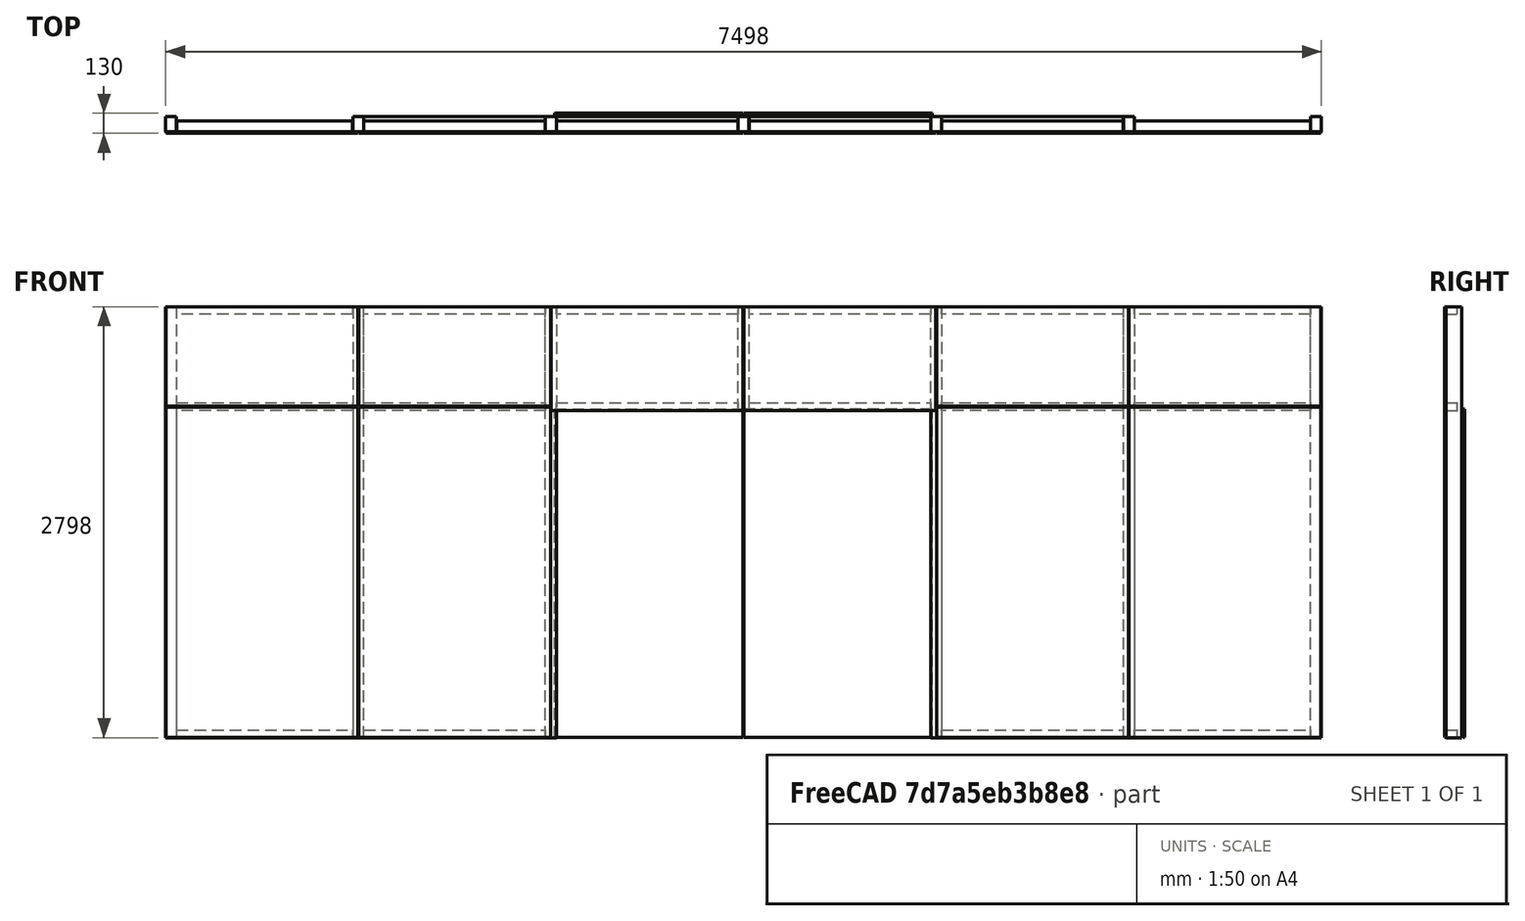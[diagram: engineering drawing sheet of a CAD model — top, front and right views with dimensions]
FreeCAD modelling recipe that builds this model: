
FCSTD DOCUMENT  (FreeCAD 0.16R6704 (Git))
Label: Glass skin 6 modules and sliding doors
License: CreativeCommons Attribution
LicenseURL: http://creativecommons.org/licenses/by/4.0/
objects: Sketcher::SketchObject×1, Part::FeaturePython×1
note: 2 computed .brp shape members not serialized (recipe doc carries the construction recipe); baked Part::Feature solids carry a one-line shape summary decoded from their .brp

FEATURE [Sketcher::SketchObject] Sketch206  label="Esboço pele de vidro 001"
  Placement = pos=(0,0,0) rot=(1,0,0;1.5708rad)
  sketch-geometry (176):
    g0: LineSegment StartX=0 StartY=0 StartZ=0 EndX=7500 EndY=0 EndZ=0
    g1: LineSegment StartX=7500 StartY=0 StartZ=0 EndX=7500 EndY=2800 EndZ=0
    g2: LineSegment StartX=7500 StartY=2800 StartZ=0 EndX=0 EndY=2800 EndZ=0
    g3: LineSegment StartX=0 StartY=2800 StartZ=0 EndX=0 EndY=0 EndZ=0
    g4: LineSegment StartX=1 StartY=2799 StartZ=0 EndX=71 EndY=2799 EndZ=0
    g5: LineSegment StartX=71 StartY=2799 StartZ=0 EndX=71 EndY=1 EndZ=0
    g6: LineSegment StartX=71 StartY=1 StartZ=0 EndX=1 EndY=1 EndZ=0
    g7: LineSegment StartX=1 StartY=1 StartZ=0 EndX=1 EndY=2799 EndZ=0
    g8: LineSegment StartX=1285 StartY=2799 StartZ=0 EndX=1215 EndY=2799 EndZ=0
    g9: LineSegment StartX=1215 StartY=2799 StartZ=0 EndX=1215 EndY=1 EndZ=0
    g10: LineSegment StartX=1215 StartY=1 StartZ=0 EndX=1285 EndY=1 EndZ=0
    g11: LineSegment StartX=1285 StartY=1 StartZ=0 EndX=1285 EndY=2799 EndZ=0
    g12: LineSegment StartX=72 StartY=2799 StartZ=0 EndX=1214 EndY=2799 EndZ=0
    g13: LineSegment StartX=1214 StartY=2799 StartZ=0 EndX=1214 EndY=2749 EndZ=0
    g14: LineSegment StartX=1214 StartY=2749 StartZ=0 EndX=72 EndY=2749 EndZ=0
    g15: LineSegment StartX=72 StartY=2749 StartZ=0 EndX=72 EndY=2799 EndZ=0
    g16: LineSegment StartX=72 StartY=2175 StartZ=0 EndX=1214 EndY=2175 EndZ=0
    g17: LineSegment StartX=1214 StartY=2175 StartZ=0 EndX=1214 EndY=2125 EndZ=0
    g18: LineSegment StartX=1214 StartY=2125 StartZ=0 EndX=72 EndY=2125 EndZ=0
    g19: LineSegment StartX=72 StartY=2125 StartZ=0 EndX=72 EndY=2175 EndZ=0
    g20: LineSegment StartX=72 StartY=51 StartZ=0 EndX=1214 EndY=51 EndZ=0
    g21: LineSegment StartX=1214 StartY=51 StartZ=0 EndX=1214 EndY=1 EndZ=0
    g22: LineSegment StartX=1214 StartY=1 StartZ=0 EndX=72 EndY=1 EndZ=0
    g23: LineSegment StartX=72 StartY=1 StartZ=0 EndX=72 EndY=51 EndZ=0
    g24: LineSegment [constr] StartX=0 StartY=4045.56 StartZ=0 EndX=0 EndY=0 EndZ=0
    g25: LineSegment [constr] StartX=1250 StartY=4032 StartZ=0 EndX=1250 EndY=-1064.23 EndZ=0
    g26: LineSegment [constr] StartX=2500 StartY=4059.26 StartZ=0 EndX=2500 EndY=-1119 EndZ=0
    g27: LineSegment [constr] StartX=3750 StartY=3908.57 StartZ=0 EndX=3750 EndY=-1023 EndZ=0
    g28: LineSegment [constr] StartX=5000 StartY=3990.77 StartZ=0 EndX=5000 EndY=-934.695 EndZ=0
    g29: LineSegment [constr] StartX=6250 StartY=4286.35 StartZ=0 EndX=6250 EndY=-1160 EndZ=0
    g30: LineSegment [constr] StartX=7500 StartY=4004.47 StartZ=0 EndX=7500 EndY=0 EndZ=0
    g31: LineSegment [constr] StartX=973.983 StartY=2150 StartZ=0 EndX=-10832.6 EndY=2150 EndZ=0
    g32: LineSegment [constr] StartX=0 StartY=3388 StartZ=0 EndX=1250 EndY=3388 EndZ=0
    g33: LineSegment [constr] StartX=1250 StartY=3579.79 StartZ=0 EndX=2500 EndY=3579.79 EndZ=0
    g34: LineSegment [constr] StartX=2500 StartY=3223.61 StartZ=0 EndX=3750 EndY=3223.61 EndZ=0
    g35: LineSegment [constr] StartX=3750 StartY=3538.69 StartZ=0 EndX=5000 EndY=3538.69 EndZ=0
    g36: LineSegment [constr] StartX=5000 StartY=3210 StartZ=0 EndX=6250 EndY=3210 EndZ=0
    g37: LineSegment [constr] StartX=6250 StartY=3579.79 StartZ=0 EndX=7500 EndY=3579.79 EndZ=0
    g38: LineSegment [constr] StartX=287.264 StartY=2799 StartZ=0 EndX=287.264 EndY=2749 EndZ=0
    g39: LineSegment [constr] StartX=559.643 StartY=2175 StartZ=0 EndX=559.643 EndY=2125 EndZ=0
    g40: LineSegment [constr] StartX=1 StartY=2367.03 StartZ=0 EndX=71 EndY=2367.03 EndZ=0
    g41: LineSegment [constr] StartX=1215 StartY=2396.22 StartZ=0 EndX=1285 EndY=2396.22 EndZ=0
    g42: LineSegment [constr] StartX=456.696 StartY=51 StartZ=0 EndX=456.696 EndY=1 EndZ=0
    g43: LineSegment StartX=2.5 StartY=2797.5 StartZ=0 EndX=1247.5 EndY=2797.5 EndZ=0
    g44: LineSegment StartX=1247.5 StartY=2797.5 StartZ=0 EndX=1247.5 EndY=2152.5 EndZ=0
    g45: LineSegment StartX=1247.5 StartY=2152.5 StartZ=0 EndX=2.5 EndY=2152.5 EndZ=0
    g46: LineSegment StartX=2.5 StartY=2152.5 StartZ=0 EndX=2.5 EndY=2797.5 EndZ=0
    g47: LineSegment StartX=2465 StartY=2799 StartZ=0 EndX=2535 EndY=2799 EndZ=0
    g48: LineSegment StartX=2535 StartY=2799 StartZ=0 EndX=2535 EndY=1 EndZ=0
    g49: LineSegment StartX=2535 StartY=1 StartZ=0 EndX=2465 EndY=1 EndZ=0
    g50: LineSegment StartX=2465 StartY=1 StartZ=0 EndX=2465 EndY=2799 EndZ=0
    g51: LineSegment StartX=3715 StartY=2799 StartZ=0 EndX=3785 EndY=2799 EndZ=0
    g52: LineSegment StartX=3785 StartY=2799 StartZ=0 EndX=3785 EndY=2125 EndZ=0
    g53: LineSegment StartX=3785 StartY=2125 StartZ=0 EndX=3715 EndY=2125 EndZ=0
    g54: LineSegment StartX=3715 StartY=2125 StartZ=0 EndX=3715 EndY=2799 EndZ=0
    g55: LineSegment StartX=4965 StartY=2799 StartZ=0 EndX=5035 EndY=2799 EndZ=0
    g56: LineSegment StartX=5035 StartY=2799 StartZ=0 EndX=5035 EndY=1 EndZ=0
    g57: LineSegment StartX=5035 StartY=1 StartZ=0 EndX=4965 EndY=1 EndZ=0
    g58: LineSegment StartX=4965 StartY=1 StartZ=0 EndX=4965 EndY=2799 EndZ=0
    g59: LineSegment StartX=6215 StartY=2799 StartZ=0 EndX=6285 EndY=2799 EndZ=0
    g60: LineSegment StartX=6285 StartY=2799 StartZ=0 EndX=6285 EndY=1 EndZ=0
    g61: LineSegment StartX=6285 StartY=1 StartZ=0 EndX=6215 EndY=1 EndZ=0
    g62: LineSegment StartX=6215 StartY=1 StartZ=0 EndX=6215 EndY=2799 EndZ=0
    g63: LineSegment StartX=7429 StartY=2799 StartZ=0 EndX=7499 EndY=2799 EndZ=0
    g64: LineSegment StartX=7499 StartY=2799 StartZ=0 EndX=7499 EndY=1 EndZ=0
    g65: LineSegment StartX=7499 StartY=1 StartZ=0 EndX=7429 EndY=1 EndZ=0
    g66: LineSegment StartX=7429 StartY=1 StartZ=0 EndX=7429 EndY=2799 EndZ=0
    g67: LineSegment [constr] StartX=2465 StartY=1674.46 StartZ=0 EndX=2535 EndY=1674.46 EndZ=0
    g68: LineSegment [constr] StartX=3715 StartY=1674.45 StartZ=0 EndX=3785 EndY=1674.45 EndZ=0
    g69: LineSegment [constr] StartX=4965 StartY=1669.74 StartZ=0 EndX=5035 EndY=1669.74 EndZ=0
    g70: LineSegment [constr] StartX=6215 StartY=1602 StartZ=0 EndX=6285 EndY=1602 EndZ=0
    g71: LineSegment [constr] StartX=7429 StartY=1550.78 StartZ=0 EndX=7499 EndY=1550.78 EndZ=0
    g72: LineSegment StartX=1286 StartY=2799 StartZ=0 EndX=2464 EndY=2799 EndZ=0
    g73: LineSegment StartX=2464 StartY=2799 StartZ=0 EndX=2464 EndY=2749 EndZ=0
    g74: LineSegment StartX=2464 StartY=2749 StartZ=0 EndX=1286 EndY=2749 EndZ=0
    g75: LineSegment StartX=1286 StartY=2749 StartZ=0 EndX=1286 EndY=2799 EndZ=0
    g76: LineSegment StartX=1286 StartY=2175 StartZ=0 EndX=2464 EndY=2175 EndZ=0
    g77: LineSegment StartX=2464 StartY=2175 StartZ=0 EndX=2464 EndY=2125 EndZ=0
    g78: LineSegment StartX=2464 StartY=2125 StartZ=0 EndX=1286 EndY=2125 EndZ=0
    g79: LineSegment StartX=1286 StartY=2125 StartZ=0 EndX=1286 EndY=2175 EndZ=0
    g80: LineSegment StartX=1286 StartY=51 StartZ=0 EndX=2464 EndY=51 EndZ=0
    g81: LineSegment StartX=2464 StartY=51 StartZ=0 EndX=2464 EndY=1 EndZ=0
    g82: LineSegment StartX=2464 StartY=1 StartZ=0 EndX=1286 EndY=1 EndZ=0
    g83: LineSegment StartX=1286 StartY=1 StartZ=0 EndX=1286 EndY=51 EndZ=0
    g84: LineSegment StartX=1252.5 StartY=2797.5 StartZ=0 EndX=2497.5 EndY=2797.5 EndZ=0
    g85: LineSegment StartX=2497.5 StartY=2797.5 StartZ=0 EndX=2497.5 EndY=2152.5 EndZ=0
    g86: LineSegment StartX=2497.5 StartY=2152.5 StartZ=0 EndX=1252.5 EndY=2152.5 EndZ=0
    g87: LineSegment StartX=1252.5 StartY=2152.5 StartZ=0 EndX=1252.5 EndY=2797.5 EndZ=0
    g88: LineSegment StartX=2536 StartY=2799 StartZ=0 EndX=3714 EndY=2799 EndZ=0
    g89: LineSegment StartX=3714 StartY=2799 StartZ=0 EndX=3714 EndY=2749 EndZ=0
    g90: LineSegment StartX=3714 StartY=2749 StartZ=0 EndX=2536 EndY=2749 EndZ=0
    g91: LineSegment StartX=2536 StartY=2749 StartZ=0 EndX=2536 EndY=2799 EndZ=0
    g92: LineSegment StartX=2536 StartY=2175 StartZ=0 EndX=3714 EndY=2175 EndZ=0
    g93: LineSegment StartX=3714 StartY=2175 StartZ=0 EndX=3714 EndY=2125 EndZ=0
    g94: LineSegment StartX=3714 StartY=2125 StartZ=0 EndX=2536 EndY=2125 EndZ=0
    g95: LineSegment StartX=2536 StartY=2125 StartZ=0 EndX=2536 EndY=2175 EndZ=0
    g96: LineSegment StartX=2536 StartY=51 StartZ=0 EndX=3714 EndY=51 EndZ=0
    g97: LineSegment StartX=3714 StartY=51 StartZ=0 EndX=3714 EndY=1 EndZ=0
    g98: LineSegment StartX=3714 StartY=1 StartZ=0 EndX=2536 EndY=1 EndZ=0
    g99: LineSegment StartX=2536 StartY=1 StartZ=0 EndX=2536 EndY=51 EndZ=0
    g100: LineSegment StartX=3786 StartY=2799 StartZ=0 EndX=4964 EndY=2799 EndZ=0
    g101: LineSegment StartX=4964 StartY=2799 StartZ=0 EndX=4964 EndY=2749 EndZ=0
    g102: LineSegment StartX=4964 StartY=2749 StartZ=0 EndX=3786 EndY=2749 EndZ=0
    g103: LineSegment StartX=3786 StartY=2749 StartZ=0 EndX=3786 EndY=2799 EndZ=0
    g104: LineSegment StartX=3786 StartY=2175 StartZ=0 EndX=4964 EndY=2175 EndZ=0
    g105: LineSegment StartX=4964 StartY=2175 StartZ=0 EndX=4964 EndY=2125 EndZ=0
    g106: LineSegment StartX=4964 StartY=2125 StartZ=0 EndX=3786 EndY=2125 EndZ=0
    g107: LineSegment StartX=3786 StartY=2125 StartZ=0 EndX=3786 EndY=2175 EndZ=0
    g108: LineSegment StartX=3786 StartY=51 StartZ=0 EndX=4964 EndY=51 EndZ=0
    g109: LineSegment StartX=4964 StartY=51 StartZ=0 EndX=4964 EndY=1 EndZ=0
    g110: LineSegment StartX=4964 StartY=1 StartZ=0 EndX=3786 EndY=1 EndZ=0
    g111: LineSegment StartX=3786 StartY=1 StartZ=0 EndX=3786 EndY=51 EndZ=0
    g112: LineSegment StartX=5036 StartY=2799 StartZ=0 EndX=6214 EndY=2799 EndZ=0
    g113: LineSegment StartX=6214 StartY=2799 StartZ=0 EndX=6214 EndY=2749 EndZ=0
    g114: LineSegment StartX=6214 StartY=2749 StartZ=0 EndX=5036 EndY=2749 EndZ=0
    g115: LineSegment StartX=5036 StartY=2749 StartZ=0 EndX=5036 EndY=2799 EndZ=0
    g116: LineSegment StartX=5036 StartY=2175 StartZ=0 EndX=6214 EndY=2175 EndZ=0
    g117: LineSegment StartX=6214 StartY=2175 StartZ=0 EndX=6214 EndY=2125 EndZ=0
    g118: LineSegment StartX=6214 StartY=2125 StartZ=0 EndX=5036 EndY=2125 EndZ=0
    g119: LineSegment StartX=5036 StartY=2125 StartZ=0 EndX=5036 EndY=2175 EndZ=0
    g120: LineSegment StartX=5036 StartY=51 StartZ=0 EndX=6214 EndY=51 EndZ=0
    g121: LineSegment StartX=6214 StartY=51 StartZ=0 EndX=6214 EndY=1 EndZ=0
    g122: LineSegment StartX=6214 StartY=1 StartZ=0 EndX=5036 EndY=1 EndZ=0
    g123: LineSegment StartX=5036 StartY=1 StartZ=0 EndX=5036 EndY=51 EndZ=0
    g124: LineSegment StartX=6286 StartY=2799 StartZ=0 EndX=7428 EndY=2799 EndZ=0
    g125: LineSegment StartX=7428 StartY=2799 StartZ=0 EndX=7428 EndY=2749 EndZ=0
    g126: LineSegment StartX=7428 StartY=2749 StartZ=0 EndX=6286 EndY=2749 EndZ=0
    g127: LineSegment StartX=6286 StartY=2749 StartZ=0 EndX=6286 EndY=2799 EndZ=0
    g128: LineSegment StartX=6286 StartY=2175 StartZ=0 EndX=7428 EndY=2175 EndZ=0
    g129: LineSegment StartX=7428 StartY=2175 StartZ=0 EndX=7428 EndY=2125 EndZ=0
    g130: LineSegment StartX=7428 StartY=2125 StartZ=0 EndX=6286 EndY=2125 EndZ=0
    g131: LineSegment StartX=6286 StartY=2125 StartZ=0 EndX=6286 EndY=2175 EndZ=0
    g132: LineSegment StartX=6286 StartY=51 StartZ=0 EndX=7428 EndY=51 EndZ=0
    g133: LineSegment StartX=7428 StartY=51 StartZ=0 EndX=7428 EndY=1 EndZ=0
    g134: LineSegment StartX=7428 StartY=1 StartZ=0 EndX=6286 EndY=1 EndZ=0
    g135: LineSegment StartX=6286 StartY=1 StartZ=0 EndX=6286 EndY=51 EndZ=0
    g136: LineSegment StartX=2502.5 StartY=2797.5 StartZ=0 EndX=3747.5 EndY=2797.5 EndZ=0
    g137: LineSegment StartX=3747.5 StartY=2797.5 StartZ=0 EndX=3747.5 EndY=2125 EndZ=0
    g138: LineSegment StartX=3747.5 StartY=2125 StartZ=0 EndX=2502.5 EndY=2125 EndZ=0
    g139: LineSegment StartX=2502.5 StartY=2125 StartZ=0 EndX=2502.5 EndY=2797.5 EndZ=0
    g140: LineSegment StartX=3752.5 StartY=2125 StartZ=0 EndX=4997.5 EndY=2125 EndZ=0
    g141: LineSegment StartX=4997.5 StartY=2125 StartZ=0 EndX=4997.5 EndY=2797.5 EndZ=0
    g142: LineSegment StartX=4997.5 StartY=2797.5 StartZ=0 EndX=3752.5 EndY=2797.5 EndZ=0
    g143: LineSegment StartX=3752.5 StartY=2797.5 StartZ=0 EndX=3752.5 EndY=2125 EndZ=0
    g144: LineSegment StartX=5002.5 StartY=2797.5 StartZ=0 EndX=6247.5 EndY=2797.5 EndZ=0
    g145: LineSegment StartX=6247.5 StartY=2797.5 StartZ=0 EndX=6247.5 EndY=2152.5 EndZ=0
    g146: LineSegment StartX=6247.5 StartY=2152.5 StartZ=0 EndX=5002.5 EndY=2152.5 EndZ=0
    g147: LineSegment StartX=5002.5 StartY=2152.5 StartZ=0 EndX=5002.5 EndY=2797.5 EndZ=0
    g148: LineSegment StartX=6252.5 StartY=2152.5 StartZ=0 EndX=7497.5 EndY=2152.5 EndZ=0
    g149: LineSegment StartX=7497.5 StartY=2152.5 StartZ=0 EndX=7497.5 EndY=2797.5 EndZ=0
    g150: LineSegment StartX=7497.5 StartY=2797.5 StartZ=0 EndX=6252.5 EndY=2797.5 EndZ=0
    g151: LineSegment StartX=6252.5 StartY=2797.5 StartZ=0 EndX=6252.5 EndY=2152.5 EndZ=0
    g152: LineSegment StartX=2525 StartY=2135 StartZ=0 EndX=3747.5 EndY=2135 EndZ=0
    g153: LineSegment StartX=3747.5 StartY=2135 StartZ=0 EndX=3747.5 EndY=2.5 EndZ=0
    g154: LineSegment StartX=3747.5 StartY=2.5 StartZ=0 EndX=2525 EndY=2.5 EndZ=0
    g155: LineSegment StartX=2525 StartY=2.5 StartZ=0 EndX=2525 EndY=2135 EndZ=0
    g156: LineSegment StartX=3752.5 StartY=2.5 StartZ=0 EndX=4975 EndY=2.5 EndZ=0
    g157: LineSegment StartX=4975 StartY=2.5 StartZ=0 EndX=4975 EndY=2135 EndZ=0
    g158: LineSegment StartX=4975 StartY=2135 StartZ=0 EndX=3752.5 EndY=2135 EndZ=0
    g159: LineSegment StartX=3752.5 StartY=2135 StartZ=0 EndX=3752.5 EndY=2.5 EndZ=0
    g160: LineSegment StartX=2.5 StartY=2147.5 StartZ=0 EndX=1247.5 EndY=2147.5 EndZ=0
    g161: LineSegment StartX=1247.5 StartY=2147.5 StartZ=0 EndX=1247.5 EndY=2.5 EndZ=0
    g162: LineSegment StartX=1247.5 StartY=2.5 StartZ=0 EndX=2.5 EndY=2.5 EndZ=0
    g163: LineSegment StartX=2.5 StartY=2.5 StartZ=0 EndX=2.5 EndY=2147.5 EndZ=0
    g164: LineSegment StartX=1252.5 StartY=2147.5 StartZ=0 EndX=2497.5 EndY=2147.5 EndZ=0
    g165: LineSegment StartX=2497.5 StartY=2147.5 StartZ=0 EndX=2497.5 EndY=2.5 EndZ=0
    g166: LineSegment StartX=2497.5 StartY=2.5 StartZ=0 EndX=1252.5 EndY=2.5 EndZ=0
    g167: LineSegment StartX=1252.5 StartY=2.5 StartZ=0 EndX=1252.5 EndY=2147.5 EndZ=0
    g168: LineSegment StartX=5002.5 StartY=2147.5 StartZ=0 EndX=6247.5 EndY=2147.5 EndZ=0
    g169: LineSegment StartX=6247.5 StartY=2147.5 StartZ=0 EndX=6247.5 EndY=2.5 EndZ=0
    g170: LineSegment StartX=6247.5 StartY=2.5 StartZ=0 EndX=5002.5 EndY=2.5 EndZ=0
    g171: LineSegment StartX=5002.5 StartY=2.5 StartZ=0 EndX=5002.5 EndY=2147.5 EndZ=0
    g172: LineSegment StartX=6252.5 StartY=2147.5 StartZ=0 EndX=7497.5 EndY=2147.5 EndZ=0
    g173: LineSegment StartX=7497.5 StartY=2147.5 StartZ=0 EndX=7497.5 EndY=2.5 EndZ=0
    g174: LineSegment StartX=7497.5 StartY=2.5 StartZ=0 EndX=6252.5 EndY=2.5 EndZ=0
    g175: LineSegment StartX=6252.5 StartY=2.5 StartZ=0 EndX=6252.5 EndY=2147.5 EndZ=0
  constraints (510):
    c: Coincident(g0,g1)
    c: Coincident(g1,g2)
    c: Coincident(g2,g3)
    c: Coincident(g3,g0)
    c: Horizontal(g0)
    c: Horizontal(g2)
    c: Vertical(g1)
    c: Vertical(g3)
    c: Coincident(g0,g-1)
    c: DistanceX(g2,g1) = 7500  'Largura do vão'
    c: DistanceY(g-1,g2) = 2800  'Altura do vão'
    c: Coincident(g4,g5)
    c: Coincident(g5,g6)
    c: Coincident(g6,g7)
    c: Coincident(g7,g4)
    c: Horizontal(g4)
    c: Horizontal(g6)
    c: Vertical(g5)
    c: Vertical(g7)
    c: Coincident(g8,g9)
    c: Coincident(g9,g10)
    c: Coincident(g10,g11)
    c: Coincident(g11,g8)
    c: Horizontal(g8)
    c: Horizontal(g10)
    c: Vertical(g9)
    c: Vertical(g11)
    c: Coincident(g12,g13)
    c: Coincident(g13,g14)
    c: Coincident(g14,g15)
    c: Coincident(g15,g12)
    c: Horizontal(g12)
    c: Horizontal(g14)
    c: Vertical(g13)
    c: Vertical(g15)
    c: Coincident(g16,g17)
    c: Coincident(g17,g18)
    c: Coincident(g18,g19)
    c: Coincident(g19,g16)
    c: Horizontal(g16)
    c: Horizontal(g18)
    c: Vertical(g17)
    c: Vertical(g19)
    c: Coincident(g20,g21)
    c: Coincident(g21,g22)
    c: Coincident(g22,g23)
    c: Coincident(g23,g20)
    c: Horizontal(g20)
    c: Horizontal(g22)
    c: Vertical(g21)
    c: Vertical(g23)
    c: Vertical(g24)
    c: Vertical(g30)
    c: PointOnObject(g32,g24)
    c: PointOnObject(g32,g25)
    c: PointOnObject(g33,g25)
    c: PointOnObject(g33,g26)
    c: PointOnObject(g34,g26)
    c: PointOnObject(g34,g27)
    c: PointOnObject(g35,g27)
    c: PointOnObject(g35,g28)
    c: PointOnObject(g36,g28)
    c: PointOnObject(g36,g29)
    c: PointOnObject(g37,g29)
    c: PointOnObject(g37,g30)
    c: Equal(g32,g33)
    c: Equal(g33,g34)
    c: Equal(g34,g35)
    c: Equal(g35,g36)
    c: Equal(g36,g37)
    c: Angle(g32) = 0
    c: Angle(g33) = 0
    c: Angle(g34) = 0
    c: Angle(g35) = 0
    c: Angle(g36) = 0
    c: Angle(g37) = 0
    c: Coincident(g24,g-1)
    c: Coincident(g30,g0)
    c: DistanceY(g-1,g31) = 2150  'Altura da divisão horizontal (eixo)'
    c: Symmetric(g16,g18,g31)  'Constraint85'
    c: Symmetric(g8,g8,g25)  'Constraint84'
    c: DistanceY(g12,g2) = 1  'Constraint83'
    c: DistanceY(g14,g12) = 50  'Altura dos perfis horizontais'
    c: DistanceX(g16,g14) = 0  'Constraint88'
    c: PointOnObject(g38,g12)  'Constraint87'
    c: PointOnObject(g38,g14)  'Constraint86'
    c: PointOnObject(g39,g16)
    c: PointOnObject(g39,g18)
    c: Angle(g38) = -1.5708
    c: Angle(g39) = -1.5708
    c: DistanceX(g2,g4) = 1
    c: DistanceY(g4,g2) = 1
    c: DistanceY(g-1,g6) = 1
    c: DistanceX(g4,g4) = 70  'Largura perfis verticais'
    c: PointOnObject(g40,g7)  'Constraint101'
    c: PointOnObject(g40,g5)
    c: Angle(g40) = 0
    c: DistanceX(g4,g12) = 1
    c: PointOnObject(g41,g9)
    c: PointOnObject(g41,g11)
    c: Angle(g41) = 0
    c: DistanceY(g8,g4) = 0
    c: DistanceY(g5,g9) = 0
    c: PointOnObject(g42,g20)
    c: PointOnObject(g42,g22)
    c: Angle(g42) = -1.5708
    c: DistanceX(g20,g18) = 0
    c: DistanceY(g5,g22) = 0
    c: Equal(g38,g39)
    c: Equal(g39,g42)
    c: DistanceX(g12,g8) = 1
    c: DistanceX(g13,g16) = 0
    c: DistanceX(g17,g20) = 0
    c: Coincident(g43,g44)
    c: Coincident(g44,g45)
    c: Coincident(g45,g46)
    c: Coincident(g46,g43)
    c: Horizontal(g43)
    c: Horizontal(g45)
    c: Vertical(g44)
    c: Vertical(g46)
    c: DistanceY(g43,g4) = 1.5
    c: DistanceX(g4,g43) = 1.5
    c: Coincident(g47,g48)
    c: Coincident(g48,g49)
    c: Coincident(g49,g50)
    c: Coincident(g50,g47)
    c: Horizontal(g47)
    c: Horizontal(g49)
    c: Vertical(g48)
    c: Vertical(g50)
    c: Coincident(g51,g52)
    c: Coincident(g52,g53)
    c: Coincident(g53,g54)
    c: Coincident(g54,g51)
    c: Horizontal(g51)
    c: Horizontal(g53)
    c: Vertical(g52)
    c: Vertical(g54)
    c: Coincident(g55,g56)
    c: Coincident(g56,g57)
    c: Coincident(g57,g58)
    c: Coincident(g58,g55)
    c: Horizontal(g55)
    c: Horizontal(g57)
    c: Vertical(g56)
    c: Vertical(g58)
    c: Coincident(g59,g60)
    c: Coincident(g60,g61)
    c: Coincident(g61,g62)
    c: Coincident(g62,g59)
    c: Horizontal(g59)
    c: Horizontal(g61)
    c: Vertical(g60)
    c: Vertical(g62)
    c: Coincident(g63,g64)
    c: Coincident(g64,g65)
    c: Coincident(g65,g66)
    c: Coincident(g66,g63)
    c: Horizontal(g63)
    c: Horizontal(g65)
    c: Vertical(g64)
    c: Vertical(g66)
    c: DistanceY(g47,g8) = 0
    c: Symmetric(g47,g47,g26)
    c: DistanceY(g51,g47) = 0
    c: Symmetric(g51,g51,g27)
    c: DistanceY(g55,g51) = 0
    c: Symmetric(g55,g55,g28)
    c: DistanceY(g55,g59) = 0
    c: Symmetric(g59,g59,g29)
    c: DistanceY(g63,g59) = 0
    c: DistanceX(g63,g1) = 1
    c: DistanceY(g10,g49) = 0
    c: DistanceY(g56,g61) = 0
    c: DistanceY(g60,g65) = 0
    c: PointOnObject(g67,g50)
    c: PointOnObject(g67,g48)
    c: PointOnObject(g68,g54)
    c: PointOnObject(g68,g52)
    c: PointOnObject(g69,g58)
    c: PointOnObject(g69,g56)
    c: PointOnObject(g70,g62)
    c: PointOnObject(g70,g60)
    c: PointOnObject(g71,g66)
    c: PointOnObject(g71,g64)
    c: Angle(g71) = 0
    c: Angle(g70) = 0
    c: Angle(g69) = 0
    c: Angle(g68) = 0
    c: Angle(g67) = 0
    c: Equal(g40,g41)
    c: Equal(g41,g67)
    c: Equal(g67,g68)
    c: Equal(g68,g69)
    c: Equal(g69,g70)
    c: Equal(g70,g71)
    c: Coincident(g72,g73)
    c: Coincident(g73,g74)
    c: Coincident(g74,g75)
    c: Coincident(g75,g72)
    c: Horizontal(g72)
    c: Horizontal(g74)
    c: Vertical(g73)
    c: Vertical(g75)
    c: Coincident(g76,g77)
    c: Coincident(g77,g78)
    c: Coincident(g78,g79)
    c: Coincident(g79,g76)
    c: Horizontal(g76)
    c: Horizontal(g78)
    c: Vertical(g77)
    c: Vertical(g79)
    c: Coincident(g80,g81)
    c: Coincident(g81,g82)
    c: Coincident(g82,g83)
    c: Coincident(g83,g80)
    c: Horizontal(g80)
    c: Horizontal(g82)
    c: Vertical(g81)
    c: Vertical(g83)
    c: DistanceX(g8,g72) = 1
    c: DistanceY(g72,g12) = 0
    c: DistanceY(g74,g13) = 0
    c: DistanceX(g74,g76) = 0
    c: DistanceY(g16,g76) = 0
    c: DistanceY(g78,g17) = 0
    c: DistanceX(g78,g80) = 0
    c: DistanceY(g21,g82) = 0
    c: DistanceY(g20,g80) = 0
    c: DistanceX(g72,g47) = 1
    c: DistanceX(g76,g73) = 0
    c: DistanceX(g80,g77) = 0
    c: Coincident(g84,g85)
    c: Coincident(g85,g86)
    c: Coincident(g86,g87)
    c: Coincident(g87,g84)
    c: Horizontal(g84)
    c: Horizontal(g86)
    c: Vertical(g85)
    c: Vertical(g87)
    c: DistanceY(g84,g43) = 0
    c: DistanceY(g44,g86) = 0
    c: Symmetric(g44,g86,g25)
    c: DistanceX(g44,g86) = 5
    c: Coincident(g88,g89)
    c: Coincident(g89,g90)
    c: Coincident(g90,g91)
    c: Coincident(g91,g88)
    c: Horizontal(g88)
    c: Horizontal(g90)
    c: Vertical(g89)
    c: Vertical(g91)
    c: Coincident(g92,g93)
    c: Coincident(g93,g94)
    c: Coincident(g94,g95)
    c: Coincident(g95,g92)
    c: Horizontal(g92)
    c: Horizontal(g94)
    c: Vertical(g93)
    c: Vertical(g95)
    c: Coincident(g96,g97)
    c: Coincident(g97,g98)
    c: Coincident(g98,g99)
    c: Coincident(g99,g96)
    c: Horizontal(g96)
    c: Horizontal(g98)
    c: Vertical(g97)
    c: Vertical(g99)
    c: Coincident(g100,g101)
    c: Coincident(g101,g102)
    c: Coincident(g102,g103)
    c: Coincident(g103,g100)
    c: Horizontal(g100)
    c: Horizontal(g102)
    c: Vertical(g101)
    c: Vertical(g103)
    c: Coincident(g104,g105)
    c: Coincident(g105,g106)
    c: Coincident(g106,g107)
    c: Coincident(g107,g104)
    c: Horizontal(g104)
    c: Horizontal(g106)
    c: Vertical(g105)
    c: Vertical(g107)
    c: Coincident(g108,g109)
    c: Coincident(g109,g110)
    c: Coincident(g110,g111)
    c: Coincident(g111,g108)
    c: Horizontal(g108)
    c: Horizontal(g110)
    c: Vertical(g109)
    c: Vertical(g111)
    c: Coincident(g112,g113)
    c: Coincident(g113,g114)
    c: Coincident(g114,g115)
    c: Coincident(g115,g112)
    c: Horizontal(g112)
    c: Horizontal(g114)
    c: Vertical(g113)
    c: Vertical(g115)
    c: Coincident(g116,g117)
    c: Coincident(g117,g118)
    c: Coincident(g118,g119)
    c: Coincident(g119,g116)
    c: Horizontal(g116)
    c: Horizontal(g118)
    c: Vertical(g117)
    c: Vertical(g119)
    c: Coincident(g120,g121)
    c: Coincident(g121,g122)
    c: Coincident(g122,g123)
    c: Coincident(g123,g120)
    c: Horizontal(g120)
    c: Horizontal(g122)
    c: Vertical(g121)
    c: Vertical(g123)
    c: Coincident(g124,g125)
    c: Coincident(g125,g126)
    c: Coincident(g126,g127)
    c: Coincident(g127,g124)
    c: Horizontal(g124)
    c: Horizontal(g126)
    c: Vertical(g125)
    c: Vertical(g127)
    c: Coincident(g128,g129)
    c: Coincident(g129,g130)
    c: Coincident(g130,g131)
    c: Coincident(g131,g128)
    c: Horizontal(g128)
    c: Horizontal(g130)
    c: Vertical(g129)
    c: Vertical(g131)
    c: Coincident(g132,g133)
    c: Coincident(g133,g134)
    c: Coincident(g134,g135)
    c: Coincident(g135,g132)
    c: Horizontal(g132)
    c: Horizontal(g134)
    c: Vertical(g133)
    c: Vertical(g135)
    c: DistanceX(g47,g88) = 1
    c: DistanceY(g88,g72) = 0
    c: DistanceY(g90,g73) = 0
    c: DistanceX(g90,g92) = 0
    c: DistanceY(g76,g92) = 0
    c: DistanceY(g94,g77) = 0
    c: DistanceX(g94,g96) = 0
    c: DistanceY(g80,g96) = 0
    c: DistanceY(g81,g98) = 0
    c: DistanceX(g88,g51) = 1
    c: DistanceX(g92,g89) = 0
    c: DistanceX(g96,g93) = 0
    c: DistanceX(g51,g100) = 1
    c: DistanceY(g100,g88) = 0
    c: DistanceY(g102,g89) = 0
    c: DistanceX(g102,g104) = 0
    c: DistanceY(g92,g104) = 0
    c: DistanceY(g106,g93) = 0
    c: DistanceX(g106,g108) = 0
    c: DistanceY(g96,g108) = 0
    c: DistanceX(g100,g55) = 1
    c: DistanceX(g104,g101) = 0
    c: DistanceX(g108,g105) = 0
    c: DistanceX(g55,g112) = 1
    c: DistanceY(g112,g100) = 0
    c: DistanceY(g114,g101) = 0
    c: DistanceX(g114,g116) = 0
    c: DistanceY(g104,g116) = 0
    c: DistanceY(g118,g105) = 0
    c: DistanceX(g118,g120) = 0
    c: DistanceY(g108,g120) = 0
    c: DistanceX(g112,g59) = 1
    c: DistanceX(g116,g113) = 0
    c: DistanceX(g120,g117) = 0
    c: DistanceX(g59,g124) = 1
    c: DistanceY(g124,g112) = 0
    c: DistanceY(g126,g113) = 0
    c: DistanceX(g126,g128) = 0
    c: DistanceY(g116,g128) = 0
    c: DistanceY(g130,g117) = 0
    c: DistanceX(g130,g132) = 0
    c: DistanceY(g120,g132) = 0
    c: DistanceY(g121,g134) = 0
    c: DistanceX(g124,g63) = 1
    c: DistanceX(g128,g125) = 0
    c: DistanceX(g132,g129) = 0
    c: Coincident(g136,g137)
    c: Coincident(g137,g138)
    c: Coincident(g138,g139)
    c: Coincident(g139,g136)
    c: Horizontal(g136)
    c: Horizontal(g138)
    c: Vertical(g137)
    c: Vertical(g139)
    c: Coincident(g140,g141)
    c: Coincident(g141,g142)
    c: Coincident(g142,g143)
    c: Coincident(g143,g140)
    c: Horizontal(g140)
    c: Horizontal(g142)
    c: Vertical(g141)
    c: Vertical(g143)
    c: Coincident(g144,g145)
    c: Coincident(g145,g146)
    c: Coincident(g146,g147)
    c: Coincident(g147,g144)
    c: Horizontal(g144)
    c: Horizontal(g146)
    c: Vertical(g145)
    c: Vertical(g147)
    c: Coincident(g148,g149)
    c: Coincident(g149,g150)
    c: Coincident(g150,g151)
    c: Coincident(g151,g148)
    c: Horizontal(g148)
    c: Horizontal(g150)
    c: Vertical(g149)
    c: Vertical(g151)
    c: DistanceY(g136,g84) = 0
    c: DistanceX(g84,g136) = 5
    c: Symmetric(g84,g136,g26)
    c: DistanceY(g142,g136) = 0
    c: Symmetric(g136,g142,g27)
    c: DistanceX(g136,g142) = 5
    c: DistanceY(g137,g140) = 0
    c: DistanceY(g144,g141) = 0
    c: Symmetric(g141,g144,g28)
    c: DistanceX(g141,g144) = 5
    c: DistanceY(g150,g144) = 0
    c: Symmetric(g144,g150,g29)
    c: DistanceX(g144,g150) = 5
    c: DistanceY(g145,g148) = 0
    c: DistanceX(g149,g63) = 1.5
    c: DistanceY(g77,g138) = 0
    c: Coincident(g152,g153)
    c: Coincident(g153,g154)
    c: Coincident(g154,g155)
    c: Coincident(g155,g152)
    c: Horizontal(g152)
    c: Horizontal(g154)
    c: Vertical(g153)
    c: Vertical(g155)
    c: Coincident(g156,g157)
    c: Coincident(g157,g158)
    c: Coincident(g158,g159)
    c: Coincident(g159,g156)
    c: Horizontal(g156)
    c: Horizontal(g158)
    c: Vertical(g157)
    c: Vertical(g159)
    c: DistanceY(g158,g152) = 0
    c: Symmetric(g152,g158,g27)
    c: DistanceX(g152,g158) = 5
    c: DistanceY(g153,g156) = 0
    c: DistanceY(g53,g93) = 0
    c: DistanceY(g77,g152) = 10
    c: DistanceX(g152,g47) = 10
    c: DistanceX(g55,g157) = 10
    c: DistanceY(g146,g85) = 0
    c: Coincident(g160,g161)
    c: Coincident(g161,g162)
    c: Coincident(g162,g163)
    c: Coincident(g163,g160)
    c: Horizontal(g160)
    c: Horizontal(g162)
    c: Vertical(g161)
    c: Vertical(g163)
    c: Coincident(g164,g165)
    c: Coincident(g165,g166)
    c: Coincident(g166,g167)
    c: Coincident(g167,g164)
    c: Horizontal(g164)
    c: Horizontal(g166)
    c: Vertical(g165)
    c: Vertical(g167)
    c: Coincident(g168,g169)
    c: Coincident(g169,g170)
    c: Coincident(g170,g171)
    c: Coincident(g171,g168)
    c: Horizontal(g168)
    c: Horizontal(g170)
    c: Vertical(g169)
    c: Vertical(g171)
    c: Coincident(g172,g173)
    c: Coincident(g173,g174)
    c: Coincident(g174,g175)
    c: Coincident(g175,g172)
    c: Horizontal(g172)
    c: Horizontal(g174)
    c: Vertical(g173)
    c: Vertical(g175)
    c: DistanceX(g45,g160) = 0
    c: Symmetric(g160,g45,g31)
    c: DistanceY(g160,g45) = 5
    c: DistanceX(g160,g44) = 0
    c: DistanceY(g6,g162) = 1.5
    c: DistanceY(g164,g160) = 0
    c: DistanceX(g86,g164) = 0
    c: DistanceY(g161,g166) = 0
    c: DistanceX(g164,g85) = 0
    c: DistanceY(g168,g164) = 0
    c: DistanceX(g146,g168) = 0
    c: DistanceY(g165,g154) = 0
    c: DistanceY(g156,g170) = 0
    c: DistanceX(g168,g145) = 0
    c: DistanceY(g172,g168) = 0
    c: DistanceX(g148,g172) = 0
    c: DistanceY(g169,g174) = 0
    c: DistanceX(g172,g148) = 0
FEATURE [Part::FeaturePython] Window122  label="Glass skin 6 modules and sliding doors"  # WARN: FeaturePython — macro-defined, semantics opaque (R4)
  Base = -> Sketch206
  Height = 0
  HoleDepth = 0
  MoveWithHost = true
  Normal = (0,1,0)
  Preset = 0
  Role = 0
  Width = 0
  WindowParts = MONTANTE VERTICAL 1 | Frame | Wire1 | 100.0 | 0.0 | MONTANTE VERTICAL 2 | Frame | Wire2 | 100.0 | 0.0 | MONTANTE VERTICAL 3 | Frame | Wire7 | 100.0 | 0.0 | MONTANTE VERTICAL 4 | Frame | Wire8 | 100 | 0.0 | MONTANTE VERTICAL 5 | Frame | Wire9 | 100.0 | 0.0 | MONTANTE VERTICAL 6 | Frame | Wire10 | 100.0 | 0.0 | MONTANTE VERTICAL 7 | Frame | Wire11 | 100.0 | 0.0 | MONTANTE HORIZONTAL 1 | Frame | Wire3 | 70.0 | 0.0 | MONTANTE HORIZONTAL 2 | Frame | Wire4 | 70.0 | 0.0 | MONTANTE HORIZONTAL 3 | Frame | Wire5 | 70.0 | 0.0 | MONTANTE HORIZONTAL 4 | Frame | Wire12 | 70.0 | 0.0 | MONTANTE HORIZONTAL 5 | Frame | Wire13 | 100.0 | 0.0 | MONTANTE HORIZONTAL 6 | Frame | Wire14 | 100.0 | 0.0 | MONTANTE HORIZONTAL 7 | Frame | Wire16 | 70.0 | 0.0 | MONTANTE HORIZONTAL 8 | Frame | Wire17 | 100.0 | 0.0 | MONTANTE HORIZONTAL 10 | Frame | Wire19 | 70.0 | 0.0 | MONTANTE HORIZONTAL 11 | Frame | Wire20 | 100.0 | 0.0 | MONTANTE HORIZONTAL 13 | Frame | Wire22 | 70.0 | 0.0 | MONTANTE HORIZONTAL 14 | Frame | Wire23 | 100.0 | 0.0 | MONTANTE HORIZONTAL 15 | Frame | Wire24 | 100.0 | 0.0 | MONTANTE HORIZONTAL 16 | Frame | Wire25 | 70.0 | 0.0 | MONTANTE HORIZONTAL 17 | Frame | Wire26 | 70.0 | 0.0 | MONTANTE HORIZONTAL 18 | Frame | Wire27 | 70.0 | 0.0 | VIDRO 1 | Glass panel | Wire6 | 10.0 | -10.0 | VIDRO 2 | Glass panel | Wire15 | 10.0 | -10.0 | VIDRO 3 | Glass panel | Wire28 | 10.0 | -10.0 | VIDRO 4 | Glass panel | Wire29 | 10.0 | -10.0 | VIDRO 5 | Glass panel | Wire30 | 10.0 | -10.0 | VIDRO 6 | Glass panel | Wire31 | 10.0 | -10.0 | PORTA 1 | Glass panel | Wire32 | 10.0 | 110.0 | PORTA 2 | Glass panel | Wire33 | 10.0 | 110.0 | VIDRO 7 | Glass panel | Wire34 | 10.0 | -10.0 | VIDRO 8 | Glass panel | Wire35 | 10.0 | -10.0 | VIDRO 9 | Glass panel | Wire36 | 10.0 | -10.0 | VIDRO 10 | Glass panel | Wire37 | 10.0 | -10.0
